# Revit family: Ekeby Bench HPL - F
name_source: partatom
category: Furniture
units: mm (PartAtom-declared; Revit-internal decimal feet)

## family parameters
Always vertical = Yes
Cut with Voids When Loaded = No
OmniClass Number = 23.21.23.13.15
Room Calculation Point = No
Shared = No
Work Plane-Based = No

## types (6) — shared parameters
BIMobject category = Bench & Park Bench
Body material = Hags - HPL FB
Description = HPL Ekeby
Edition number = 1
IFC Classification = Furniture
Manufacturer = Hags
Manufacturer name = HAGS
OmniClass Code = 23-21 23 13 15
OmniClass Description = Residential Sofas
Product Guid = 90e49432-c870-4a59-897e-b15016e8f9bd
Product url = https://www.hags.com
QR code = https://www.hags.com
URL = https://www.hags.com
Uniclass 1.4 Code = L8211
Uniclass 1.4 Description = Furniture
zero-valued in all types: Default Elevation

## per-type parameters (varying)
| type | Body material_90 | Construction material | Model | Product name |
| 8101204 Green/ Galvanised | Hags - HPL Green | Hags - Steel - Galvanized | 8101204 | Ekeby Bench HPL Green/Galvanised - F |
| 8101199 Green/ Black | Hags - HPL Green | Hags - Steel - Powder coated - Black | 8101199 | Ekeby Bench HPL Green/Black - F |
| 8101205 Grey/ Galvanised | Hags - HPL Grey | Hags - Steel - Galvanized | 8101205 | Ekeby Bench HPL Grey/Galvanised - F |
| 8101201 Grey/ Black | Hags - HPL Grey | Hags - Steel - Powder coated - Black | 8101201 | Ekeby Bench HPL Grey/Black - F |
| 8101207 Beige/ Galvanised | Hags - HPL Beige | Hags - Steel - Galvanized | 8101207 | Ekeby Bench HPL Beige/Galvanised - F |
| 8101202 Beige/ Black | Hags - HPL Beige | Hags - Steel - Powder coated - Black | 8101202 | Ekeby Bench HPL Beige/Black - F |

## geometry (parser evidence)
native form markers: Sweep x3
no freeform markers — native parametric forms only
